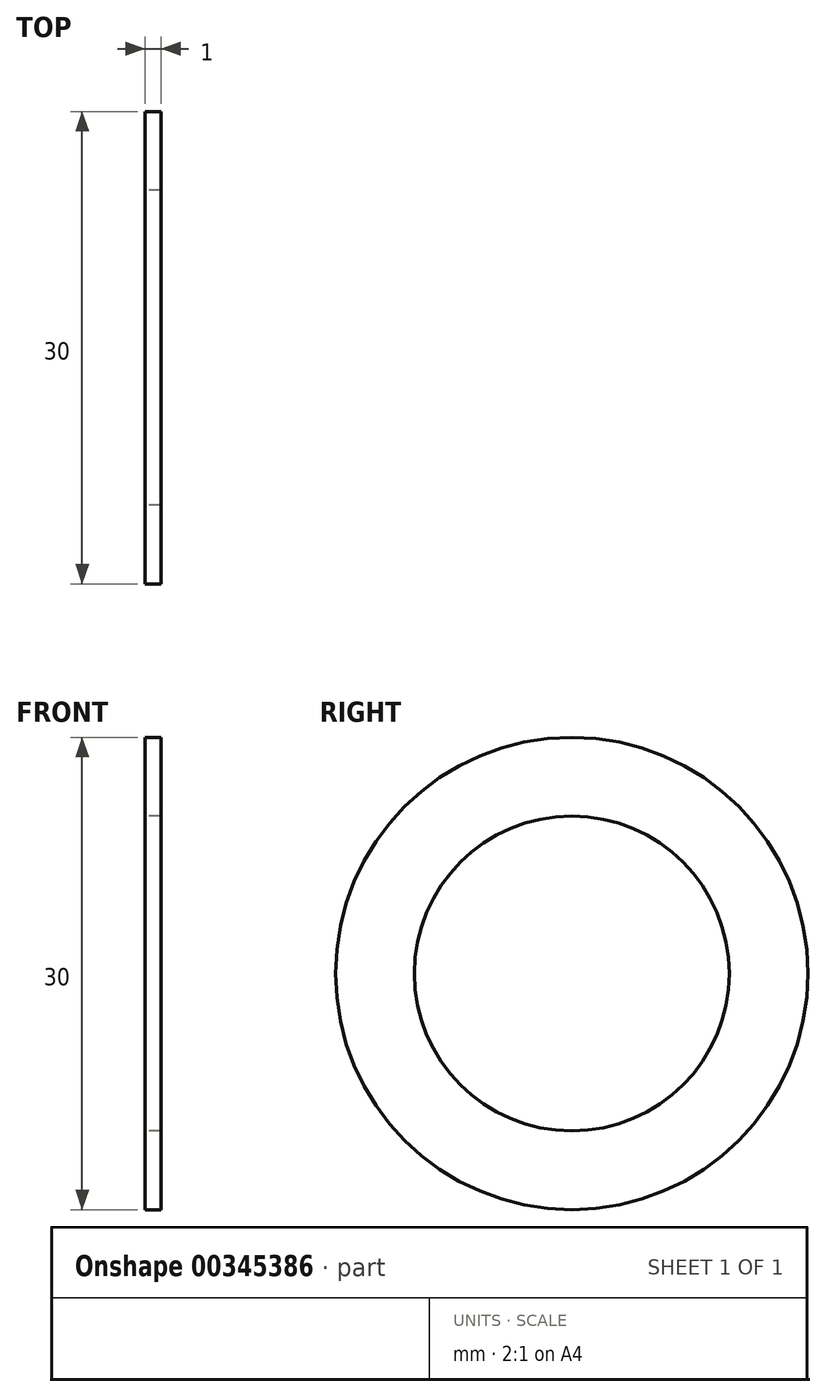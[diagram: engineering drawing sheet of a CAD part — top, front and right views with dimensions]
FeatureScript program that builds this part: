
annotation { "Feature Type Name" : "Feature", "Feature Type Description" : "" }
export const myFeature = defineFeature(function(context is Context, id is Id, definition is map)
    precondition{}
    {
        {
            var Q0;
            Q0=qCreatedBy(makeId("Right.planeOp"),FACE);
            var sketch = newSketch(context, id + "F0", { "sketchPlane" : qUnion([Q0])});
            skCircle(sketch, "E0", {"center": v(0, 0) * mm, "radius": 15 * mm});
            skCircle(sketch, "E1", {"center": v(0, 0) * mm, "radius": 10 * mm});
            skSolve(sketch);
        }
        {
            var Q0;
            Q0 = qSketchRegion(id + "F0", true);
            extrude(context, id + "F1", {"entities" : qUnion([Q0]), "depth" : 1 * mm});
        }
    });
